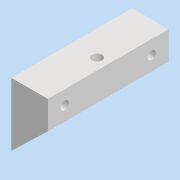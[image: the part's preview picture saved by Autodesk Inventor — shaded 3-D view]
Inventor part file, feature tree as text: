
AUTODESK INVENTOR PART (.ipt)
format: ipt  version: 2020 (Build 240168000, 168)  size: 133,120 bytes
history: native  units: mm
features: sketch x5, extrude x3, hole x2
ambient origin geometry x8: Origin, YZ Plane, XZ Plane, XY Plane, X Axis, Y Axis, Z Axis, Center Point
bodies: Solido1 (feature_tree)
feature tree (10):
  extrude  "Estrusione1"  Depth=26.0mm
  extrude  "Estrusione2"  Depth=86.0mm
  extrude  "Estrusione3"  Depth=20.0mm TaperAngle=0.0deg
  hole  "Foro1"  [1 undecoded]
  hole  "Foro2"  [1 undecoded]
  sketch  "Schizzo1"
  sketch  "Schizzo2"
  sketch  "Schizzo3"
  sketch  "Schizzo4"
  sketch  "Schizzo5"
note: 2 required parameter values undecoded (feature->parameter linkage not recoverable at this tier; creation-order binding heuristic only, values carry confidence <= 0.55)
